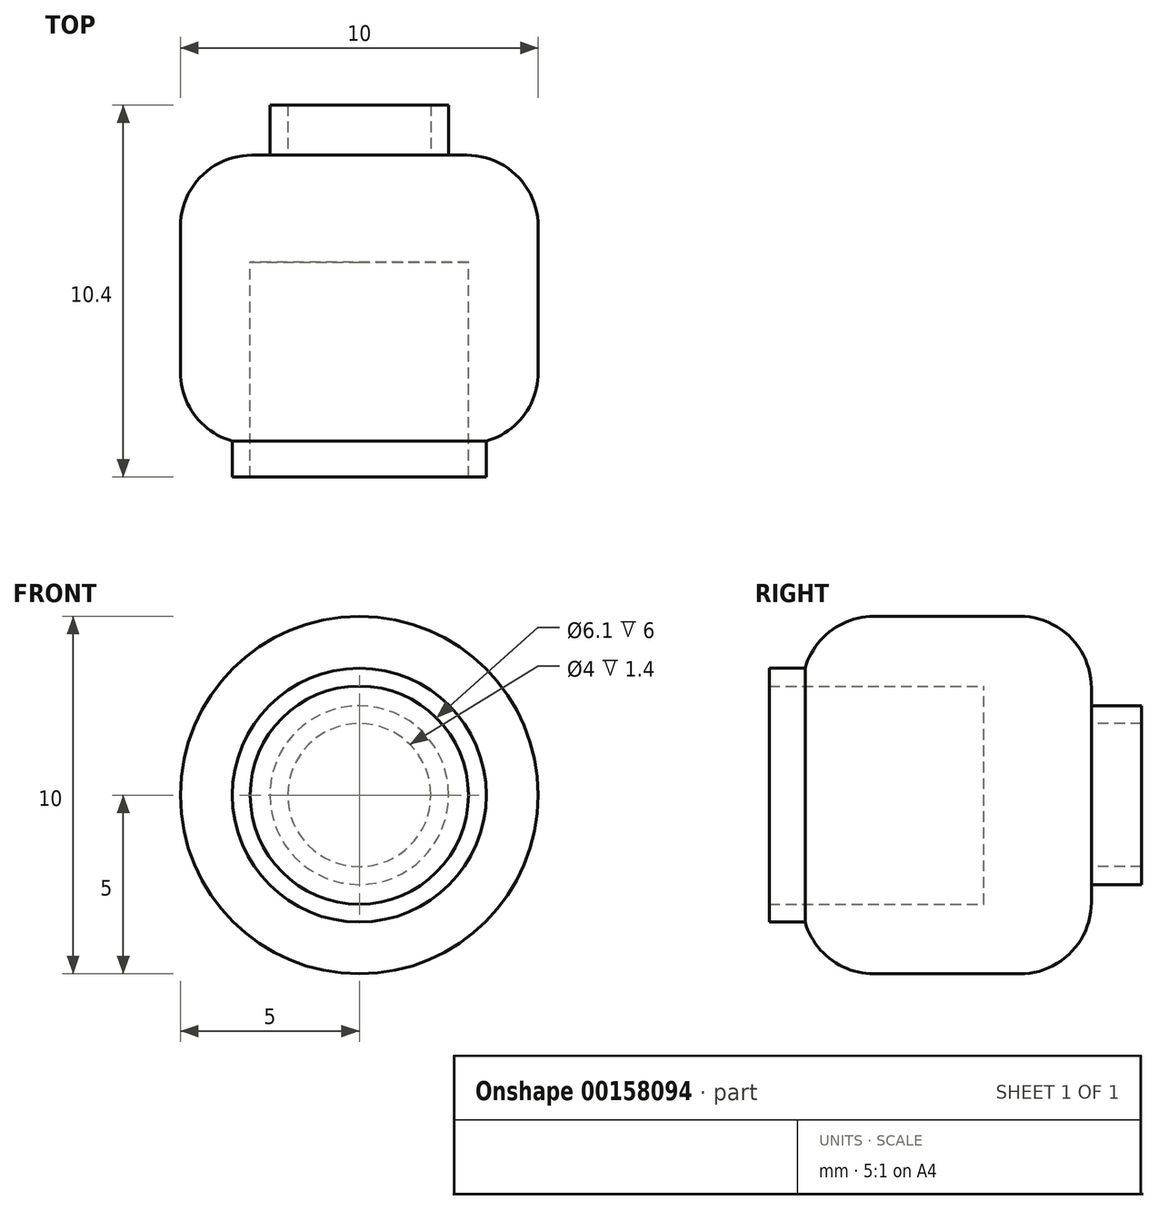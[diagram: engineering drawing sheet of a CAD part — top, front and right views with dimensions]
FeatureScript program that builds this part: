
annotation { "Feature Type Name" : "Feature", "Feature Type Description" : "" }
export const myFeature = defineFeature(function(context is Context, id is Id, definition is map)
    precondition{}
    {
        {
            var Q0;
            Q0=qCreatedBy(makeId("Front.planeOp"),FACE);
            var sketch = newSketch(context, id + "F0", { "sketchPlane" : qUnion([Q0])});
            skCircle(sketch, "E0", {"center": v(0, 0) * mm, "radius": 3.05 * mm});
            skCircle(sketch, "E1", {"center": v(0, 0) * mm, "radius": 3.55 * mm});
            skSolve(sketch);
        }
        {
            var Q0;
            Q0=makeQuery(id+"F0.imprint","IMPRINT",FACE,{"disambiguationData":[TD([[makeQuery(id+"F0.imprint","IMPRINT",EDGE,{"derivedFrom":sQuery(id+"F0.wireOp",EDGE,"E0")}),-1.0]])]});
            extrude(context, id + "F1", {"entities" : qUnion([Q0]), "depth" : 1 * mm});
        }
        {
            var Q0;
            Q0=qCreatedBy(makeId("Front.planeOp"),FACE);
            var sketch = newSketch(context, id + "F2", { "sketchPlane" : qUnion([Q0])});
            skCircle(sketch, "E2", {"center": v(0, 0) * mm, "radius": 5 * mm});
            skSolve(sketch);
        }
        {
            var Q0;
            Q0=makeQuery(id+"F2.imprint","IMPRINT",FACE,{"disambiguationData":[TD([[makeQuery(id+"F2.imprint","IMPRINT",EDGE,{"derivedFrom":sQuery(id+"F2.wireOp",EDGE,"E2")}),1.0]])]});
            extrude(context, id + "F3", {"entities" : qUnion([Q0]), "operationType" : NewBodyOperationType.ADD, "oppositeDirection" : true, "depth" : 8 * mm});
        }
        {
            var Q0;
            Q0=makeQuery(id+"F3.opExtrude","CAP_FACE",FACE,{"disambiguationData":[OSD([sQuery(id+"F2.wireOp",EDGE,"E2")])],"isStart":false});
            var sketch = newSketch(context, id + "F4", { "sketchPlane" : qUnion([Q0])});
            skSolve(sketch);
        }
        {
            var Q0;
            Q0=makeQuery(id+"F4.imprint","IMPRINT",FACE,{"disambiguationData":[TD([[makeQuery(id+"F4.imprint","IMPRINT",EDGE,{"derivedFrom":makeQuery(id+"F3.opExtrude","CAP_EDGE",EDGE,{"disambiguationData":[OSD([sQuery(id+"F2.wireOp",EDGE,"E2")])],"isStart":false})}),-1.0]])]});
            var sketch = newSketch(context, id + "F5", { "sketchPlane" : qUnion([Q0])});
            skCircle(sketch, "E3", {"center": v(0, 0) * mm, "radius": 2.5 * mm});
            skCircle(sketch, "E4", {"center": v(0, 0) * mm, "radius": 2 * mm});
            skSolve(sketch);
        }
        {
            var Q0;
            Q0=makeQuery(id+"F5.imprint","IMPRINT",FACE,{"disambiguationData":[TD([[makeQuery(id+"F5.imprint","IMPRINT",EDGE,{"derivedFrom":sQuery(id+"F5.wireOp",EDGE,"E3")}),1.0]])]});
            extrude(context, id + "F6", {"entities" : qUnion([Q0]), "operationType" : NewBodyOperationType.ADD, "depth" : 1.4 * mm});
        }
        {
            var Q0;
            Q0=makeQuery(id+"F3.opExtrude","CAP_EDGE",EDGE,{"disambiguationData":[OSD([sQuery(id+"F2.wireOp",EDGE,"E2")])],"isStart":false});
            var Q1;
            Q1=makeQuery(id+"F3.opExtrude","CAP_EDGE",EDGE,{"disambiguationData":[OSD([sQuery(id+"F2.wireOp",EDGE,"E2")])],"isStart":true});
            fillet(context, id + "F7", {"entities" : qUnion([Q0, Q1]), "radius" : 2 * mm, "tangentPropagation" : true, "allowEdgeOverflow" : false});
        }
        {
            var Q0;
            Q0=makeQuery(id+"F3.boolean.opBoolean","SPLIT",FACE,{"disambiguationData":[TD([makeQuery(id+"F1.opExtrude","SWEPT_FACE",FACE,{"disambiguationData":[OSD([sQuery(id+"F0.wireOp",EDGE,"E0")])]})])],"derivedFrom":makeQuery(id+"F3.opExtrude","CAP_FACE",FACE,{"disambiguationData":[OSD([sQuery(id+"F2.wireOp",EDGE,"E2")])],"isStart":true})});
            extrude(context, id + "F8", {"entities" : qUnion([Q0]), "operationType" : NewBodyOperationType.REMOVE, "oppositeDirection" : true, "depth" : 5 * mm});
        }
    });
